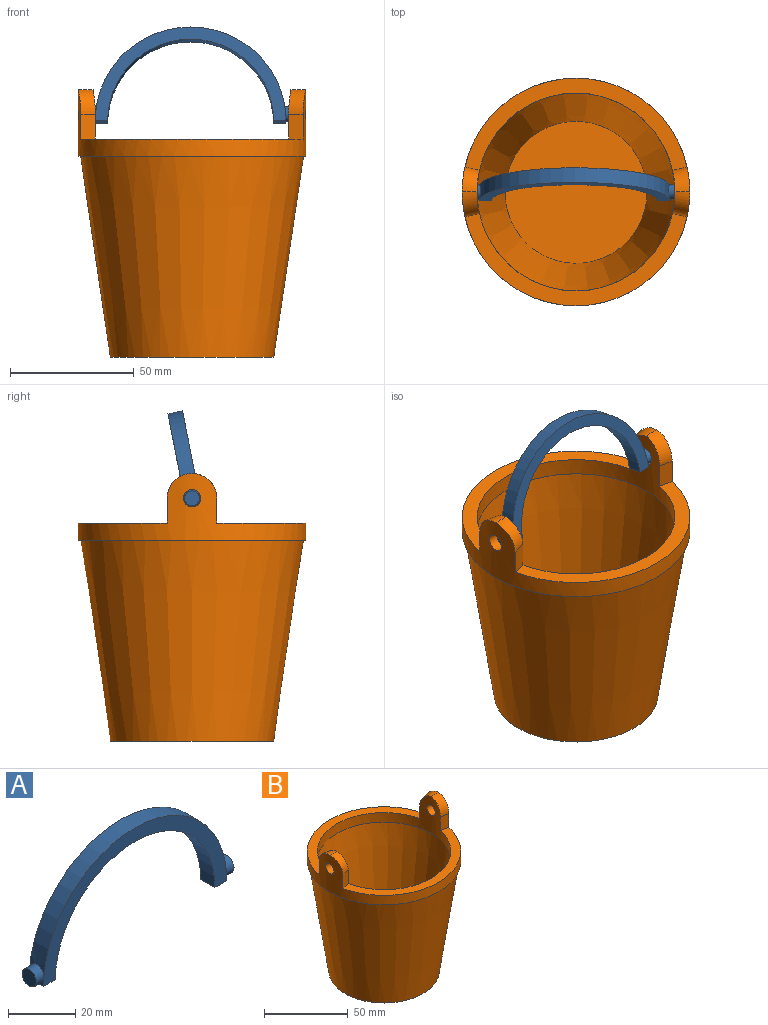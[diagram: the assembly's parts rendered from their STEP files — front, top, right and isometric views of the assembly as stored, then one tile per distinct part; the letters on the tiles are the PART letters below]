
ASSEMBLY  parts=2 mates=1
PART A: 12 faces, bbox 83x6x38.5 mm
  f0: cylinder r=38.5mm len=6mm, axis (0,1,0), area 5mm2, adj f3,f6,f7,f10
  f1: cylinder r=38.5mm len=6mm, axis (0,1,0), area 5mm2, adj f5,f6,f7,f9
  f2: cylinder r=38.5mm len=76.74mm, axis (0,1,0), area 659mm2, adj f6,f7,f9,f10
  f3: plane 6x5mm, normal (0,0,-1), area 30mm2, adj f0,f4,f6,f7
  f4: cylinder r=33.5mm len=67mm, axis (0,1,0), area 631.5mm2, adj f3,f5,f6,f7
  f5: plane 6x5mm, normal (0,0,-1), area 30mm2, adj f1,f4,f6,f7
  f6: plane 77x38.5mm, normal (0,-1,0), area 565.5mm2, adj f0,f1,f2,f3,f4,f5
  f7: plane 77x38.5mm, normal (0,1,0), area 565.5mm2, adj f0,f1,f2,f3,f4,f5
  f8: plane 6x6mm, normal (1,0,0), area 28.3mm2, adj f9
  f9: cylinder r=3mm len=6mm, axis (-1,0,0), area 60.2mm2, adj f1,f2,f8
  f10: cylinder r=3mm len=6mm, axis (1,0,0), area 60.2mm2, adj f0,f2,f11
  f11: plane 6x6mm, normal (-1,0,0), area 28.3mm2, adj f10
PART B: 19 faces, bbox 94x91.9x108 mm
  f0: plane 89.69x37.25mm, normal (0,0,1), area 696.4mm2, adj f7,f8,f10,f14
  f1: plane 89.69x37.25mm, normal (0,0,1), area 696.4mm2, adj f7,f8,f9,f13
  f2: cone r=39.95mm half-angle=8.4deg, axis (0,0,1), area 16565.4mm2, adj f3,f8
  f3: plane 57.37x57.37mm, normal (0,0,1), area 2585.2mm2, adj f2
  f4: plane 66x66mm, normal (0,0,-1), area 3421.2mm2, adj f5
  f5: cone r=33mm half-angle=8.4deg, axis (0,0,1), area 20065.2mm2, adj f4,f6
  f6: plane 91.89x91.89mm, normal (0,0,-1), area 270.1mm2, adj f5,f7
  f7: cylinder r=45.95mm len=91.89mm, axis (0,0,1), area 2664.1mm2, adj f0,f1,f6,f9,f10,f11,f12,f13
  f8: cylinder r=39.95mm len=79.89mm, axis (0,0,1), area 2295.2mm2, adj f0,f1,f2,f9,f10,f11,f12,f13
  f9: plane 10x5.86mm, normal (-0.22,0.98,0), area 60mm2, adj f1,f7,f8,f11
  f10: plane 10x5.86mm, normal (-0.22,-0.98,0), area 60mm2, adj f0,f7,f8,f12
  f11: cylinder r=10mm len=11.27mm, axis (0.98,0.22,0), area 90.8mm2, adj f7,f8,f9,f12
  f12: cylinder r=10mm len=11.27mm, axis (-0.98,0.22,0), area 90.8mm2, adj f7,f8,f10,f11
  f13: plane 10x5.86mm, normal (0.22,0.98,0), area 60mm2, adj f1,f7,f8,f15
  f14: plane 10x5.86mm, normal (0.22,-0.98,0), area 60mm2, adj f0,f7,f8,f16
  f15: cylinder r=10mm len=11.27mm, axis (0.98,-0.22,0), area 90.8mm2, adj f7,f8,f13,f16
  f16: cylinder r=10mm len=11.27mm, axis (-0.98,-0.22,0), area 90.8mm2, adj f7,f8,f14,f15
  f17: cylinder r=3.5mm len=7mm, axis (1,0,0), area 132.2mm2, adj f7,f8
  f18: cylinder r=3.5mm len=7mm, axis (1,0,0), area 132.2mm2, adj f7,f8
PLACE A rot(axis=(-1,0,0),11deg) t=(-0.57,2.34,94.3)mm
PLACE B at identity fixed
MATE cylindrical A.f9 <-> B.f17  axis (1,0,0) through (40.93,0,98)mm
